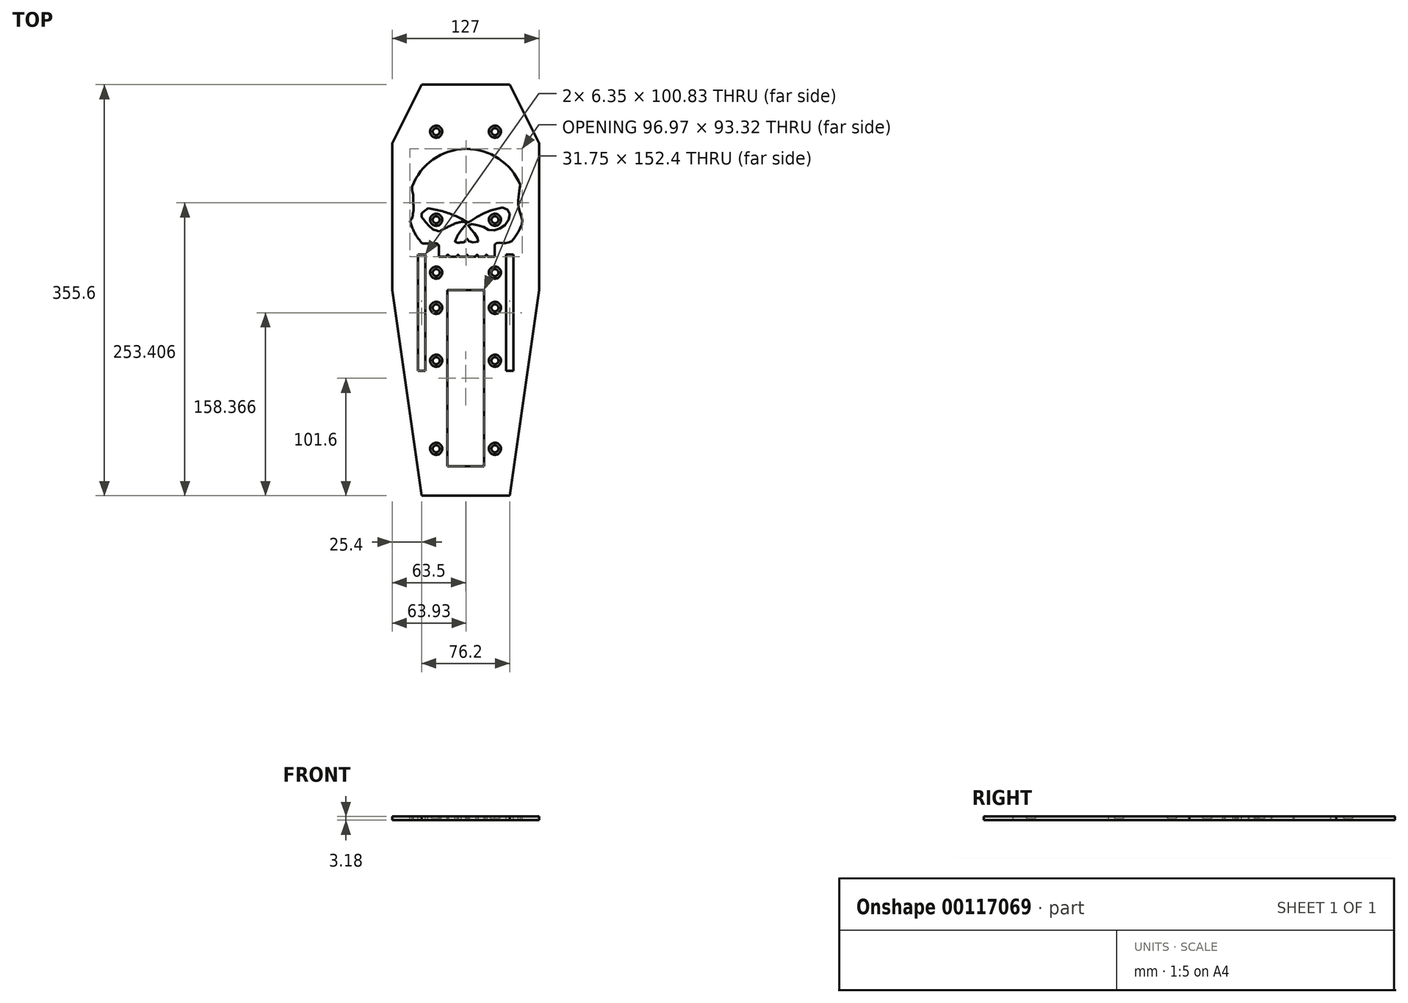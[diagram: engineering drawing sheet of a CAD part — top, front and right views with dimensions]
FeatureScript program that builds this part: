
annotation { "Feature Type Name" : "Feature", "Feature Type Description" : "" }
export const myFeature = defineFeature(function(context is Context, id is Id, definition is map)
    precondition{}
    {
        {
            var Q0;
            Q0=qCreatedBy(makeId("Top.planeOp"),FACE);
            var sketch = newSketch(context, id + "F0", { "sketchPlane" : qUnion([Q0])});
            skLineSegment(sketch, "E0", {"start": v(63.5, 0) * mm, "end": v(38.1, -177.8) * mm});
            skLineSegment(sketch, "E1.MirrorCS", {"start": v(-63.5, 0) * mm, "end": v(-38.1, -177.8) * mm});
            skLineSegment(sketch, "E2", {"start": v(38.1, -177.8) * mm, "end": v(-38.1, -177.8) * mm});
            skLineSegment(sketch, "E3", {"start": v(-63.5, 127) * mm, "end": v(-38.1, 177.8) * mm});
            skLineSegment(sketch, "E4.MirrorCS", {"start": v(63.5, 127) * mm, "end": v(38.1, 177.8) * mm});
            skLineSegment(sketch, "E5", {"start": v(-38.1, 177.8) * mm, "end": v(38.1, 177.8) * mm});
            skLineSegment(sketch, "E6", {"start": v(63.5, 127) * mm, "end": v(63.5, 0) * mm});
            skLineSegment(sketch, "E7", {"start": v(-63.5, 127) * mm, "end": v(-63.5, 0) * mm});
            skSolve(sketch);
        }
        {
            var Q0;
            Q0=qSketchRegion(id+"F0",true);
            extrude(context, id + "F1", {"entities" : qUnion([Q0]), "depth" : 3.17 * mm});
        }
        {
            var Q0;
            Q0=makeQuery(id+"F1.opExtrude","CAP_FACE",FACE,{"disambiguationData":[OSD([sQuery(id+"F0.wireOp",EDGE,"E0"),sQuery(id+"F0.wireOp",EDGE,"E1.MirrorCS"),sQuery(id+"F0.wireOp",EDGE,"6Zdo3cuH-ixeM-oXwf-qIJs-YBNe2MJ6Rbqx"),sQuery(id+"F0.wireOp",EDGE,"747895df-24c0-4a9d-9004-2816c155ee1e0.MirrorCS"),sQuery(id+"F0.wireOp",EDGE,"VV5kUZRL-BcaJ-A9Ud-53TX-DaUSXjS1JonS"),sQuery(id+"F0.wireOp",EDGE,"KG54DKq3-Zvdh-Th0P-ERyz-S8xl1YFJODya"),sQuery(id+"F0.wireOp",EDGE,"r76tLJJg-OteC-Wcak-jAAw-e4UhULwSnmC2"),sQuery(id+"F0.wireOp",EDGE,"E2"),sQuery(id+"F0.wireOp",EDGE,"l3t51EjR-4HDC-blX0-KO7P-OmxVzPPfY23m"),sQuery(id+"F0.wireOp",EDGE,"QA2xfThh-9Ufp-mOM6-GMJK-7phE9abyktDD")])],"isStart":false});
            var sketch = newSketch(context, id + "F2", { "sketchPlane" : qUnion([Q0])});
            skArc(sketch, "E8", {"start": v(47.4, 90.81) * mm, "mid": v(0.22, 122.27) * mm, "end": v(-46.2, 89.68) * mm});
            skFitSpline(sketch, "E9", {"points": [v(-48.05, 60.27) * mm, v(-46.59, 61.84) * mm, v(-45.8, 64.44) * mm, v(-45.12, 68.84) * mm, v(-45.12, 73.4) * mm, v(-45.34, 79.3) * mm, v(-45.57, 83.74) * mm, v(-46.23, 87.4) * mm, v(-46.2, 89.68) * mm], "startDerivative": vector(17.25, 15.05) * mm, "endDerivative": vector(1.92, 21.82) * mm});
            skFitSpline(sketch, "E10", {"points": [v(-48.05, 60.27) * mm, v(-37.5, 40.57) * mm], "startDerivative": vector(6.2, -24.32) * mm, "endDerivative": vector(15.52, -16.14) * mm});
            skLineSegment(sketch, "E11", {"start": v(-37.5, 40.57) * mm, "end": v(-25.94, 40.57) * mm});
            skArc(sketch, "E12", {"start": v(-23.02, 37.53) * mm, "mid": v(-23.83, 39.67) * mm, "end": v(-25.94, 40.57) * mm});
            skLineSegment(sketch, "E13", {"start": v(-23.02, 37.53) * mm, "end": v(-23.02, 28.95) * mm});
            skLineSegment(sketch, "E14", {"start": v(25.15, 28.95) * mm, "end": v(25.15, 39.4) * mm});
            skFitSpline(sketch, "E15", {"points": [v(25.15, 39.4) * mm, v(26.86, 40.74) * mm, v(29.66, 41.16) * mm, v(32.74, 40.74) * mm, v(37.5, 41.3) * mm, v(40.45, 42.98) * mm, v(43.67, 47.6) * mm, v(46.75, 52.5) * mm, v(48.96, 59.27) * mm, v(48.13, 63.83) * mm, v(46.68, 68.15) * mm, v(45.88, 72.61) * mm, v(45.56, 76.44) * mm, v(45.72, 80.9) * mm, v(46.2, 84.42) * mm, v(46.84, 88.09) * mm, v(47.4, 90.81) * mm], "startDerivative": vector(33.43, 33.48) * mm, "endDerivative": vector(10.96, 50.43) * mm});
            skFitSpline(sketch, "E16", {"points": [v(-32.5, 70.82) * mm, v(-35.22, 68.74) * mm, v(-36.82, 67.63) * mm, v(-38.1, 65.55) * mm, v(-37.46, 62.84) * mm, v(-34.42, 58.85) * mm, v(-31.4, 55.5) * mm, v(-27.88, 52.63) * mm, v(-22.3, 51.04) * mm], "startDerivative": vector(-24.13, -19.41) * mm, "endDerivative": vector(40.6, -6.88) * mm});
            skFitSpline(sketch, "E17", {"points": [v(-22.3, 51.04) * mm, v(-18.95, 52.95) * mm, v(-16.4, 54.22) * mm, v(-11.62, 56.51) * mm, v(-7.75, 58.17) * mm, v(-3.63, 59.17) * mm], "startDerivative": vector(15.88, 11.3) * mm, "endDerivative": vector(21.24, 4.15) * mm});
            skFitSpline(sketch, "E18", {"points": [v(1.12, 45.01) * mm, v(1.7, 43.68) * mm, v(2.96, 42.26) * mm, v(4.62, 41.35) * mm, v(6.79, 41.35) * mm, v(10.2, 41.85) * mm, v(11.2, 42.26) * mm, v(11.12, 43.68) * mm, v(9.29, 46.85) * mm, v(7.46, 49.32) * mm, v(5.62, 51.51) * mm, v(3.3, 54.34) * mm, v(2.3, 55.76) * mm, v(2.62, 56.76) * mm, v(4.46, 57.26) * mm, v(7.41, 56.93) * mm, v(11.85, 55.86) * mm, v(16.28, 54.39) * mm, v(19.24, 52.5) * mm, v(23.01, 51.68) * mm, v(26.22, 52) * mm, v(30.24, 53.65) * mm, v(33.6, 55.86) * mm, v(36.28, 59.1) * mm, v(38.38, 63.88) * mm, v(38.05, 66.5) * mm, v(36.92, 68.99) * mm, v(34.59, 70.72) * mm, v(31.47, 71.46) * mm, v(30.66, 71.31) * mm, v(25.54, 70.05) * mm, v(20.27, 68.42) * mm, v(13.96, 65.75) * mm, v(8.17, 62.48) * mm, v(2.46, 58.39) * mm, v(-2.14, 54) * mm, v(-5.73, 49.31) * mm, v(-7.78, 45.51) * mm, v(-9.17, 42.44) * mm], "startDerivative": vector(27.46, -77.27) * mm, "endDerivative": vector(-50.54, -114.37) * mm});
            skFitSpline(sketch, "E19", {"points": [v(-9.17, 42.44) * mm, v(-8.8, 41.86) * mm, v(-7.75, 41.3) * mm, v(-6.54, 41.15) * mm, v(-4.26, 41.26) * mm, v(-2.27, 41.47) * mm, v(-0.57, 42.18) * mm, v(0.57, 43.92) * mm, v(1.12, 45.01) * mm], "startDerivative": vector(3.44, -7) * mm, "endDerivative": vector(4.55, 8.82) * mm});
            skFitSpline(sketch, "E20", {"points": [v(-16.02, 28.95) * mm, v(-16.18, 29.64) * mm, v(-16.07, 30.39) * mm, v(-15.4, 30.5) * mm, v(-14.66, 30.34) * mm, v(-14.7, 29.6) * mm, v(-14.87, 28.95) * mm], "startDerivative": vector(-1.15, 3.9) * mm, "endDerivative": vector(-0.84, -3.76) * mm});
            skFitSpline(sketch, "E21", {"points": [v(-7.26, 28.95) * mm, v(-7.36, 29.66) * mm, v(-7.2, 30.23) * mm, v(-6.78, 30.55) * mm, v(-6.15, 30.34) * mm, v(-5.94, 29.7) * mm, v(-6.05, 28.95) * mm], "startDerivative": vector(-0.93, 4.12) * mm, "endDerivative": vector(-0.89, -4.21) * mm});
            skFitSpline(sketch, "E22", {"points": [v(0.68, 28.95) * mm, v(0.62, 29.32) * mm, v(0.65, 29.96) * mm, v(1.06, 30.46) * mm, v(1.68, 30.4) * mm, v(1.9, 30.02) * mm, v(1.96, 29.63) * mm, v(1.85, 28.95) * mm], "startDerivative": vector(-0.5, 2.88) * mm, "endDerivative": vector(-0.98, -4.53) * mm});
            skFitSpline(sketch, "E23", {"points": [v(8.9, 28.95) * mm, v(8.87, 29.39) * mm, v(8.87, 29.95) * mm, v(9.16, 30.35) * mm, v(9.9, 30.48) * mm, v(10.37, 30.35) * mm, v(10.78, 29.92) * mm, v(10.72, 29.48) * mm, v(10.53, 28.95) * mm], "startDerivative": vector(-0.24, 3.72) * mm, "endDerivative": vector(-1.47, -4.24) * mm});
            skFitSpline(sketch, "E24", {"points": [v(17.2, 28.95) * mm, v(17.24, 29.42) * mm, v(17.24, 30.04) * mm, v(17.48, 30.35) * mm, v(17.88, 30.6) * mm, v(18.44, 30.6) * mm, v(18.8, 30.35) * mm, v(18.93, 29.8) * mm, v(18.8, 29.27) * mm, v(18.8, 28.95) * mm], "startDerivative": vector(0.52, 3.98) * mm, "endDerivative": vector(0.34, -3.4) * mm});
            skLineSegment(sketch, "E25", {"start": v(-23.02, 28.95) * mm, "end": v(-16.02, 28.95) * mm});
            skLineSegment(sketch, "E26", {"start": v(-14.87, 28.95) * mm, "end": v(-7.26, 28.95) * mm});
            skLineSegment(sketch, "E27", {"start": v(-6.05, 28.95) * mm, "end": v(0.68, 28.95) * mm});
            skLineSegment(sketch, "E28", {"start": v(1.85, 28.95) * mm, "end": v(8.9, 28.95) * mm});
            skLineSegment(sketch, "E29", {"start": v(10.53, 28.95) * mm, "end": v(17.2, 28.95) * mm});
            skLineSegment(sketch, "E30", {"start": v(18.8, 28.95) * mm, "end": v(25.15, 28.95) * mm});
            skFitSpline(sketch, "E31", {"points": [v(-32.5, 70.82) * mm, v(2.46, 58.39) * mm], "startDerivative": vector(40.7, -5.39) * mm, "endDerivative": vector(30.57, -18.18) * mm});
            skFitSpline(sketch, "E32", {"points": [v(-3.63, 59.17) * mm, v(0, 56.2) * mm], "startDerivative": vector(10.9, 1.55) * mm, "endDerivative": vector(-2.8, -4.17) * mm});
            skFitSpline(sketch, "E33", {"points": [v(0.6, 59.47) * mm, v(3.84, 59.47) * mm], "startDerivative": vector(3.76, -2.54) * mm, "endDerivative": vector(2.66, 2.17) * mm});
            skSolve(sketch);
        }
        {
            var Q0;
            Q0=qSketchRegion(id+"F2",true);
            extrude(context, id + "F3", {"entities" : qUnion([Q0]), "operationType" : NewBodyOperationType.REMOVE, "endBound" : BoundingType.THROUGH_ALL, "oppositeDirection" : true, "depth" : 25.4 * mm});
        }
        {
            var Q0;
            {var subQ0=sQuery(id+"F0.wireOp",EDGE,"E0");var subQ1=sQuery(id+"F0.wireOp",EDGE,"E3");var subQ2=sQuery(id+"F0.wireOp",EDGE,"E2");var subQ3=sQuery(id+"F0.wireOp",EDGE,"E1.MirrorCS");var subQ4=sQuery(id+"F0.wireOp",EDGE,"E5");var subQ5=sQuery(id+"F0.wireOp",EDGE,"E4.MirrorCS");var subQ6=sQuery(id+"F0.wireOp",EDGE,"E6");var subQ7=sQuery(id+"F0.wireOp",EDGE,"E7");Q0=makeQuery(id+"F3.boolean.opBoolean","SPLIT",FACE,{"disambiguationData":[TD([makeQuery(id+"F1.opExtrude","SWEPT_FACE",FACE,{"disambiguationData":[OSD([subQ0])]})])],"derivedFrom":makeQuery(id+"F1.opExtrude","CAP_FACE",FACE,{"disambiguationData":[OSD([subQ0,subQ3,subQ2,subQ1,subQ5,subQ4,subQ6,subQ7])],"isStart":false})});}
            var sketch = newSketch(context, id + "F4", { "sketchPlane" : qUnion([Q0])});
            skLineSegment(sketch, "E34", {"start": v(-34.92, -69.85) * mm, "end": v(-41.28, -69.85) * mm});
            skLineSegment(sketch, "E35", {"start": v(-15.88, -152.4) * mm, "end": v(15.88, -152.4) * mm});
            skLineSegment(sketch, "E36", {"start": v(-15.88, 0) * mm, "end": v(15.87, 0) * mm});
            skLineSegment(sketch, "E37", {"start": v(-15.88, -88.9) * mm, "end": v(15.87, -88.9) * mm});
            skLineSegment(sketch, "E38", {"start": v(-15.87, -63.5) * mm, "end": v(15.87, -63.5) * mm});
            skLineSegment(sketch, "E39", {"start": v(-15.88, 0) * mm, "end": v(-15.88, -63.5) * mm});
            skLineSegment(sketch, "E40", {"start": v(15.87, 0) * mm, "end": v(15.87, -63.5) * mm});
            skLineSegment(sketch, "E41", {"start": v(15.87, -88.9) * mm, "end": v(15.88, -152.4) * mm});
            skLineSegment(sketch, "E42", {"start": v(-15.88, -88.9) * mm, "end": v(-15.88, -152.4) * mm});
            skLineSegment(sketch, "E43", {"start": v(-34.93, 30.98) * mm, "end": v(-41.28, 30.98) * mm});
            skLineSegment(sketch, "E44", {"start": v(-34.93, 30.98) * mm, "end": v(-34.92, -69.85) * mm});
            skLineSegment(sketch, "E45", {"start": v(-41.28, 30.98) * mm, "end": v(-41.28, -69.85) * mm});
            skLineSegment(sketch, "E46.MirrorCS", {"start": v(34.93, 30.98) * mm, "end": v(41.28, 30.98) * mm});
            skLineSegment(sketch, "E47.MirrorCS", {"start": v(34.93, 30.98) * mm, "end": v(34.93, -69.85) * mm});
            skLineSegment(sketch, "E48.MirrorCS", {"start": v(41.28, 30.98) * mm, "end": v(41.28, -69.85) * mm});
            skLineSegment(sketch, "E49.MirrorCS", {"start": v(34.92, -69.85) * mm, "end": v(41.28, -69.85) * mm});
            skLineSegment(sketch, "E50", {"start": v(15.87, -63.5) * mm, "end": v(15.87, -88.9) * mm});
            skLineSegment(sketch, "E51", {"start": v(-15.88, -88.9) * mm, "end": v(-15.87, -63.5) * mm});
            skSolve(sketch);
        }
        {
            var Q0;
            Q0=qSketchRegion(id+"F4",true);
            extrude(context, id + "F5", {"entities" : qUnion([Q0]), "operationType" : NewBodyOperationType.REMOVE, "endBound" : BoundingType.THROUGH_ALL, "oppositeDirection" : true, "depth" : 25.4 * mm});
        }
        {
            var Q0;
            {var subQ0=sQuery(id+"F0.wireOp",EDGE,"E0");var subQ1=sQuery(id+"F0.wireOp",EDGE,"E3");var subQ2=sQuery(id+"F0.wireOp",EDGE,"E2");var subQ3=sQuery(id+"F0.wireOp",EDGE,"E1.MirrorCS");var subQ4=sQuery(id+"F0.wireOp",EDGE,"E5");var subQ5=sQuery(id+"F0.wireOp",EDGE,"E4.MirrorCS");var subQ6=sQuery(id+"F0.wireOp",EDGE,"E6");var subQ7=sQuery(id+"F0.wireOp",EDGE,"E7");Q0=makeQuery(id+"F3.boolean.opBoolean","SPLIT",FACE,{"disambiguationData":[TD([makeQuery(id+"F1.opExtrude","SWEPT_FACE",FACE,{"disambiguationData":[OSD([subQ0])]})])],"derivedFrom":makeQuery(id+"F1.opExtrude","CAP_FACE",FACE,{"disambiguationData":[OSD([subQ0,subQ3,subQ2,subQ1,subQ5,subQ4,subQ6,subQ7])],"isStart":false})});}
            var sketch = newSketch(context, id + "F6", { "sketchPlane" : qUnion([Q0])});
            skPoint(sketch, "E52", {"position": v(25.4, 137.16) * mm});
            skPoint(sketch, "E53", {"position": v(25.4, 60.96) * mm});
            skPoint(sketch, "E54", {"position": v(-25.4, 15.24) * mm});
            skPoint(sketch, "E55", {"position": v(25.4, 15.24) * mm});
            skPoint(sketch, "E56", {"position": v(25.4, -137.16) * mm});
            skPoint(sketch, "E57", {"position": v(-25.4, -137.16) * mm});
            skPoint(sketch, "E58", {"position": v(-25.4, 137.16) * mm});
            skPoint(sketch, "E59", {"position": v(-25.4, 60.96) * mm});
            skPoint(sketch, "E60", {"position": v(25.4, -60.96) * mm});
            skPoint(sketch, "E61", {"position": v(-25.4, -60.96) * mm});
            skPoint(sketch, "E62.MirrorP", {"position": v(-25.4, -15.24) * mm});
            skPoint(sketch, "E63.MirrorP", {"position": v(25.4, -15.24) * mm});
            skSolve(sketch);
        }
        {
            var Q0;
            Q0=sQuery(id+"F6.wireOp",VERTEX,"E58");
            var Q1;
            Q1=sQuery(id+"F6.wireOp",VERTEX,"E52");
            var Q2;
            Q2=sQuery(id+"F6.wireOp",VERTEX,"E59");
            var Q3;
            Q3=sQuery(id+"F6.wireOp",VERTEX,"E53");
            var Q4;
            Q4=sQuery(id+"F6.wireOp",VERTEX,"dcfb655d-c3de-465f-b43b-5a80e16fb3cc");
            var Q5;
            Q5=sQuery(id+"F6.wireOp",VERTEX,"E54");
            var Q6;
            Q6=sQuery(id+"F6.wireOp",VERTEX,"E55");
            var Q7;
            Q7=sQuery(id+"F6.wireOp",VERTEX,"E56");
            var Q8;
            Q8=sQuery(id+"F6.wireOp",VERTEX,"E57");
            var Q9;
            Q9=sQuery(id+"F6.wireOp",VERTEX,"E61");
            var Q10;
            Q10=sQuery(id+"F6.wireOp",VERTEX,"E60");
            var Q11;
            Q11=sQuery(id+"F6.wireOp",VERTEX,"E62.MirrorP");
            var Q12;
            Q12=sQuery(id+"F6.wireOp",VERTEX,"E63.MirrorP");
            var Q13;
            Q13=makeQuery(id+"F3.boolean.opBoolean","SPLIT",BODY,{"disambiguationData":[OD(0.0)],"derivedFrom":makeQuery(id+"F1.opExtrude","SWEPT_BODY",BODY,{"disambiguationData":[OSD([sQuery(id+"F0.wireOp",EDGE,"E0"),sQuery(id+"F0.wireOp",EDGE,"E1.MirrorCS"),sQuery(id+"F0.wireOp",EDGE,"E2"),sQuery(id+"F0.wireOp",EDGE,"E3"),sQuery(id+"F0.wireOp",EDGE,"E4.MirrorCS"),sQuery(id+"F0.wireOp",EDGE,"E5"),sQuery(id+"F0.wireOp",EDGE,"E6"),sQuery(id+"F0.wireOp",EDGE,"E7")])]})});
            var Q14;
            Q14=makeQuery(id+"F3.boolean.opBoolean","SPLIT",BODY,{"disambiguationData":[OD(1.0)],"derivedFrom":makeQuery(id+"F1.opExtrude","SWEPT_BODY",BODY,{"disambiguationData":[OSD([sQuery(id+"F0.wireOp",EDGE,"E0"),sQuery(id+"F0.wireOp",EDGE,"E1.MirrorCS"),sQuery(id+"F0.wireOp",EDGE,"E2"),sQuery(id+"F0.wireOp",EDGE,"E3"),sQuery(id+"F0.wireOp",EDGE,"E4.MirrorCS"),sQuery(id+"F0.wireOp",EDGE,"E5"),sQuery(id+"F0.wireOp",EDGE,"E6"),sQuery(id+"F0.wireOp",EDGE,"E7")])]})});
            var Q15;
            Q15=makeQuery(id+"F3.boolean.opBoolean","SPLIT",BODY,{"disambiguationData":[OD(2.0)],"derivedFrom":makeQuery(id+"F1.opExtrude","SWEPT_BODY",BODY,{"disambiguationData":[OSD([sQuery(id+"F0.wireOp",EDGE,"E0"),sQuery(id+"F0.wireOp",EDGE,"E1.MirrorCS"),sQuery(id+"F0.wireOp",EDGE,"E2"),sQuery(id+"F0.wireOp",EDGE,"E3"),sQuery(id+"F0.wireOp",EDGE,"E4.MirrorCS"),sQuery(id+"F0.wireOp",EDGE,"E5"),sQuery(id+"F0.wireOp",EDGE,"E6"),sQuery(id+"F0.wireOp",EDGE,"E7")])]})});
            hole(context, id + "F7", {"style" : HoleStyle.C_SINK, "endStyle" : HoleEndStyle.THROUGH, "holeDiameter" : 6 * mm, "cSinkDiameter" : 10.5 * mm, "cSinkAngle" : 94 * degree, "startFromSketch" : true, "locations" : qUnion([Q0, Q1, Q2, Q3, Q4, Q5, Q6, Q7, Q8, Q9, Q10, Q11, Q12]), "scope" : qUnion([Q13, Q14, Q15]), "isTappedThrough" : true});
        }
        {
            var Q0;
            Q0=qCreatedBy(makeId("Top.planeOp"),FACE);
            var sketch = newSketch(context, id + "F8", { "sketchPlane" : qUnion([Q0])});
            skLineSegment(sketch, "E64", {"start": v(77.04, 77.78) * mm, "end": v(-76.27, -75.52) * mm});
            skSolve(sketch);
        }
    });
